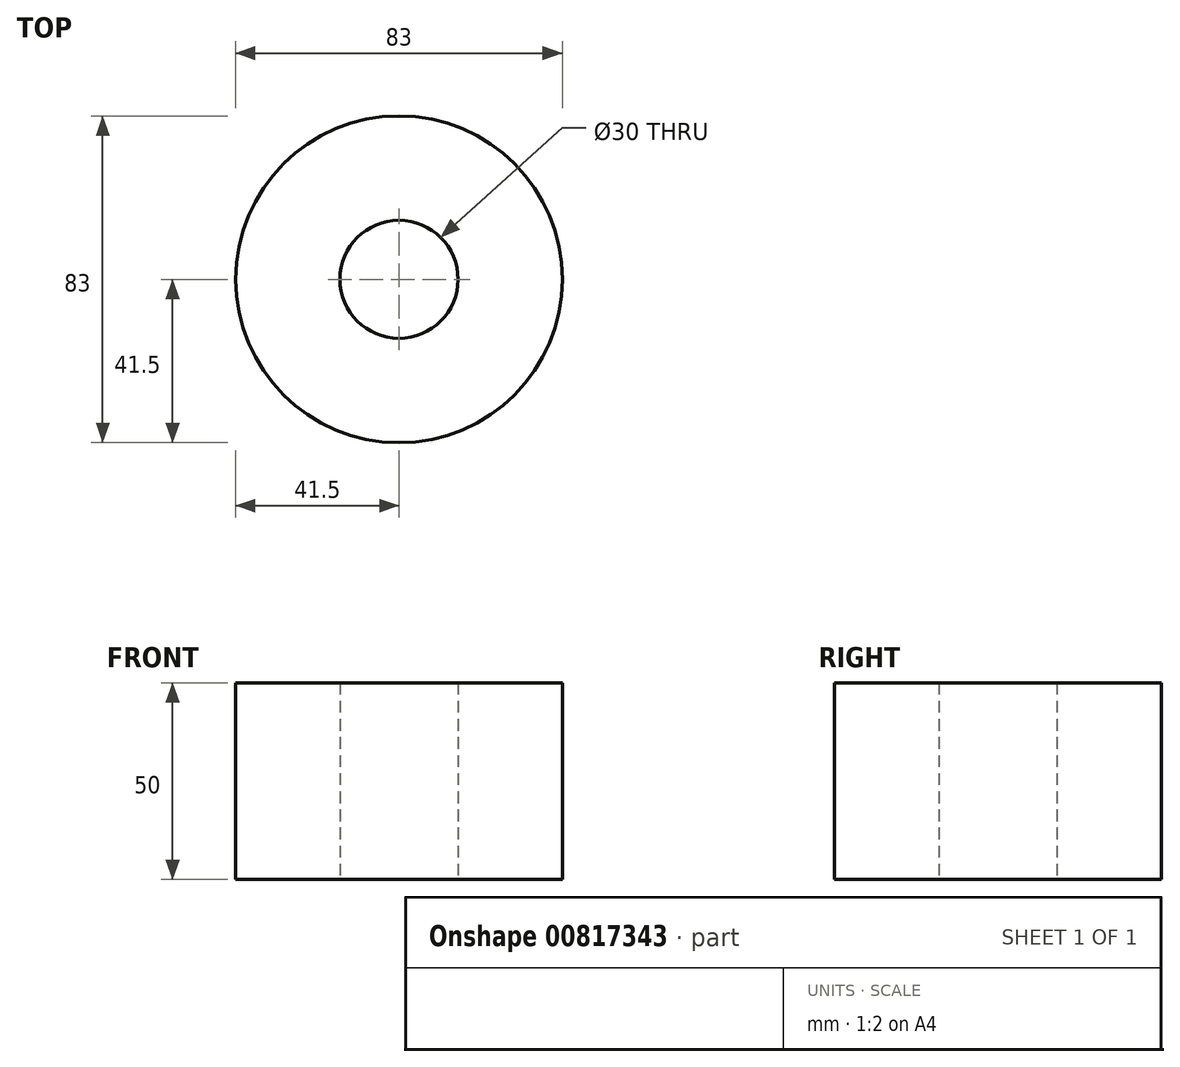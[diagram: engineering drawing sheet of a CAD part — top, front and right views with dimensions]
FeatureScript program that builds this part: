
annotation { "Feature Type Name" : "Feature", "Feature Type Description" : "" }
export const myFeature = defineFeature(function(context is Context, id is Id, definition is map)
    precondition{}
    {
        {
            var Q0;
            Q0=qCreatedBy(makeId("Top.planeOp"),FACE);
            var sketch = newSketch(context, id + "F0", { "sketchPlane" : qUnion([Q0])});
            skCircle(sketch, "E0", {"center": v(0, 0) * mm, "radius": 41.5 * mm});
            skCircle(sketch, "E1", {"center": v(0, 0) * mm, "radius": 15 * mm});
            skSolve(sketch);
        }
        {
            var Q0;
            Q0=makeQuery(id+"F0.imprint","IMPRINT",FACE,{"disambiguationData":[TD([[makeQuery(id+"F0.imprint","IMPRINT",EDGE,{"derivedFrom":sQuery(id+"F0.wireOp",EDGE,"E0")}),1.0]])]});
            extrude(context, id + "F1", {"entities" : qUnion([Q0]), "depth" : 50 * mm, "offsetDistance" : 25.4 * mm});
        }
    });
